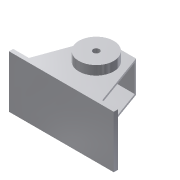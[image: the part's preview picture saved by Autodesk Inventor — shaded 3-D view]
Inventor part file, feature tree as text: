
AUTODESK INVENTOR PART (.ipt)
format: ipt  version: 2016 (Build 200138000, 138)  size: 125,440 bytes
history: native  units: mm
features: extrude x5, sketch x5
ambient origin geometry x8: Origin, YZ Plane, XZ Plane, XY Plane, X Axis, Y Axis, Z Axis, Center Point
bodies: Solid1 (feature_tree)
feature tree (10):
  extrude  "Extrusion1"  Depth=75.0mm
  extrude  "Extrusion2"  Depth=45.0mm TaperAngle=0.0deg
  extrude  "Extrusion3"  Depth=50.0mm
  extrude  "Extrusion4"  Depth=3.0mm
  extrude  "Extrusion5"  Depth=3.0mm
  sketch  "Sketch1"  dims[d0=150.0mm d1=75.0mm]
  sketch  "Sketch6"  dims[d2=6.0mm d3=0.0mm d12=45.0mm d13=0.0mm]
  sketch  "Sketch7"  dims[d14=50.0mm d15=50.0mm]
  sketch  "Sketch9"  dims[d16=13.0mm d17=0.0mm d18=3.0mm]
  sketch  "Sketch10"  dims[d19=3.0mm d20=3.0mm d21=3.0mm d22=150.0mm d23=0.0mm d24=9.0mm d25=150.0mm d26=0.0mm]
